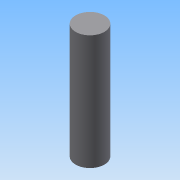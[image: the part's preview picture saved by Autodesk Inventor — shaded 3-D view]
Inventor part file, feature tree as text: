
AUTODESK INVENTOR PART (.ipt)
format: ipt  version: 2015 (Build 190159000, 159)  size: 64,512 bytes
history: native  units: mm
features: other x1, extrude x1, sketch x1
ambient origin geometry x8: Origin, YZ Plane, XZ Plane, XY Plane, X Axis, Y Axis, Z Axis, Center Point
bodies: Body1 (feature_tree)
feature tree (3):
  other  "實體1"
  extrude  "擠出1"  Depth=1.0mm
  sketch  "草圖1"
